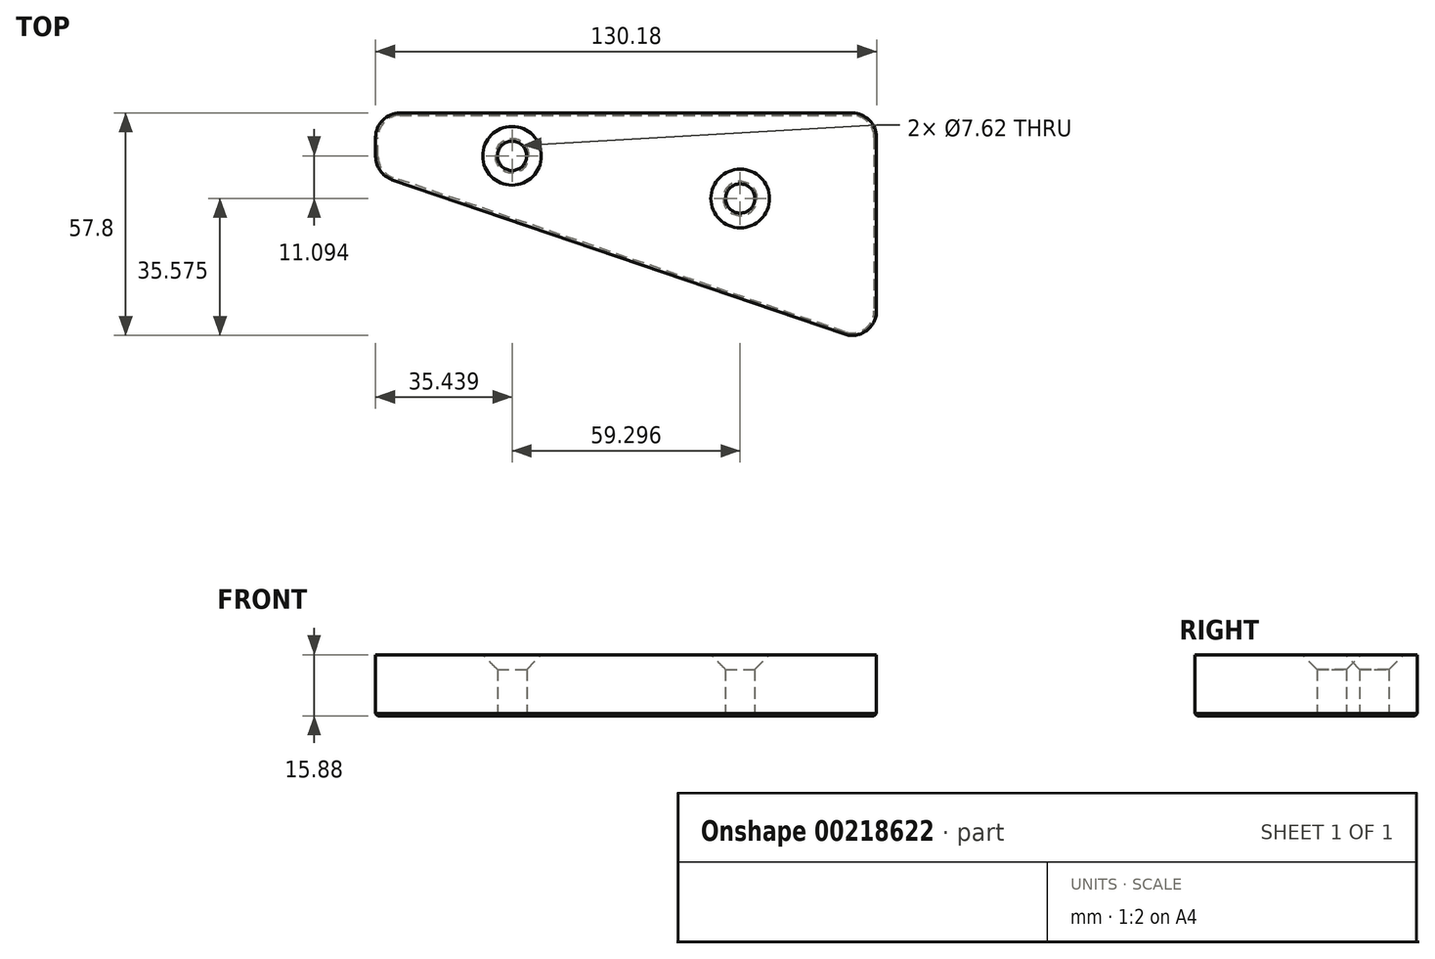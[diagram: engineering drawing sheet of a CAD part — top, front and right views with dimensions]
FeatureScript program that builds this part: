
annotation { "Feature Type Name" : "Feature", "Feature Type Description" : "" }
export const myFeature = defineFeature(function(context is Context, id is Id, definition is map)
    precondition{}
    {
        {
            var Q0;
            Q0=qCreatedBy(makeId("Top.planeOp"),FACE);
            var sketch = newSketch(context, id + "F0", { "sketchPlane" : qUnion([Q0])});
            skLineSegment(sketch, "E0", {"start": v(0, 0) * mm, "end": v(0, -15.88) * mm});
            skLineSegment(sketch, "E1", {"start": v(0, -15.88) * mm, "end": v(130.17, -60.32) * mm});
            skLineSegment(sketch, "E2", {"start": v(130.17, -60.33) * mm, "end": v(130.17, 0) * mm});
            skLineSegment(sketch, "E3", {"start": v(130.17, 0) * mm, "end": v(0, 0) * mm});
            skSolve(sketch);
        }
        {
            var Q0;
            Q0 = qSketchRegion(id + "F0", true);
            extrude(context, id + "F1", {"entities" : qUnion([Q0]), "depth" : 15.88 * mm, "offsetDistance" : 25.4 * mm});
        }
        {
            var Q0;
            Q0=makeQuery(id+"F1.opExtrude","CAP_FACE",FACE,{"disambiguationData":[OSD([sQuery(id+"F0.wireOp",EDGE,"E0"),sQuery(id+"F0.wireOp",EDGE,"E1"),sQuery(id+"F0.wireOp",EDGE,"E2"),sQuery(id+"F0.wireOp",EDGE,"E3")])],"isStart":false});
            var sketch = newSketch(context, id + "F2", { "sketchPlane" : qUnion([Q0])});
            skPoint(sketch, "E4", {"position": v(35.44, -11.13) * mm});
            skPoint(sketch, "E5", {"position": v(94.74, -22.23) * mm});
            skLineSegment(sketch, "E6", {"start": v(35.44, -11.13) * mm, "end": v(94.74, -22.23) * mm, "construction": true});
            skLineSegment(sketch, "E7", {"start": v(65.09, -16.68) * mm, "end": v(65.09, 0) * mm, "construction": true});
            skSolve(sketch);
        }
        {
            var Q0;
            Q0=sQuery(id+"F2.wireOp",VERTEX,"E4");
            var Q1;
            Q1=sQuery(id+"F2.wireOp",VERTEX,"E5");
            var Q2;
            Q2=makeQuery(id+"F1.opExtrude","SWEPT_BODY",BODY,{"disambiguationData":[OSD([sQuery(id+"F0.wireOp",EDGE,"E0"),sQuery(id+"F0.wireOp",EDGE,"E1"),sQuery(id+"F0.wireOp",EDGE,"E2"),sQuery(id+"F0.wireOp",EDGE,"E3")])]});
            hole(context, id + "F3", {"style" : HoleStyle.C_SINK, "endStyle" : HoleEndStyle.THROUGH, "holeDiameter" : 7.62 * mm, "cSinkDiameter" : 15.24 * mm, "cSinkAngle" : 90 * degree, "majorDiameter" : 6.35 * mm, "isTappedThrough" : true, "tappedDepth" : 12.7 * mm, "tapClearance" : 3, "locations" : qUnion([Q0, Q1]), "scope" : qUnion([Q2]), "startStyle" : HoleStartStyle.PART});
        }
        {
            var Q0;
            Q0=makeQuery(id+"F1.opExtrude","SWEPT_EDGE",EDGE,{"disambiguationData":[OSD([sQuery(id+"F0.wireOp",EDGE,"E0"),sQuery(id+"F0.wireOp",EDGE,"E1")])]});
            var Q1;
            Q1=makeQuery(id+"F1.opExtrude","SWEPT_EDGE",EDGE,{"disambiguationData":[OSD([sQuery(id+"F0.wireOp",EDGE,"E0"),sQuery(id+"F0.wireOp",EDGE,"E3")])]});
            var Q2;
            Q2=makeQuery(id+"F1.opExtrude","SWEPT_EDGE",EDGE,{"disambiguationData":[OSD([sQuery(id+"F0.wireOp",EDGE,"E1"),sQuery(id+"F0.wireOp",EDGE,"E2")])]});
            var Q3;
            Q3=makeQuery(id+"F1.opExtrude","SWEPT_EDGE",EDGE,{"disambiguationData":[OSD([sQuery(id+"F0.wireOp",EDGE,"E2"),sQuery(id+"F0.wireOp",EDGE,"E3")])]});
            fillet(context, id + "F4", {"entities" : qUnion([Q0, Q1, Q2, Q3]), "tangentPropagation" : true, "radius" : 6.35 * mm, "defaultsChanged" : true, "vertexSettings" : [], "allowEdgeOverflow" : false});
        }
        {
            var Q0;
            Q0=makeQuery(id+"F1.opExtrude","CAP_FACE",FACE,{"disambiguationData":[OSD([sQuery(id+"F0.wireOp",EDGE,"E0"),sQuery(id+"F0.wireOp",EDGE,"E1"),sQuery(id+"F0.wireOp",EDGE,"E2"),sQuery(id+"F0.wireOp",EDGE,"E3")])],"isStart":true});
            chamfer(context, id + "F5", {"entities" : qUnion([Q0]), "width" : 0.64 * mm, "tangentPropagation" : true});
        }
    });
